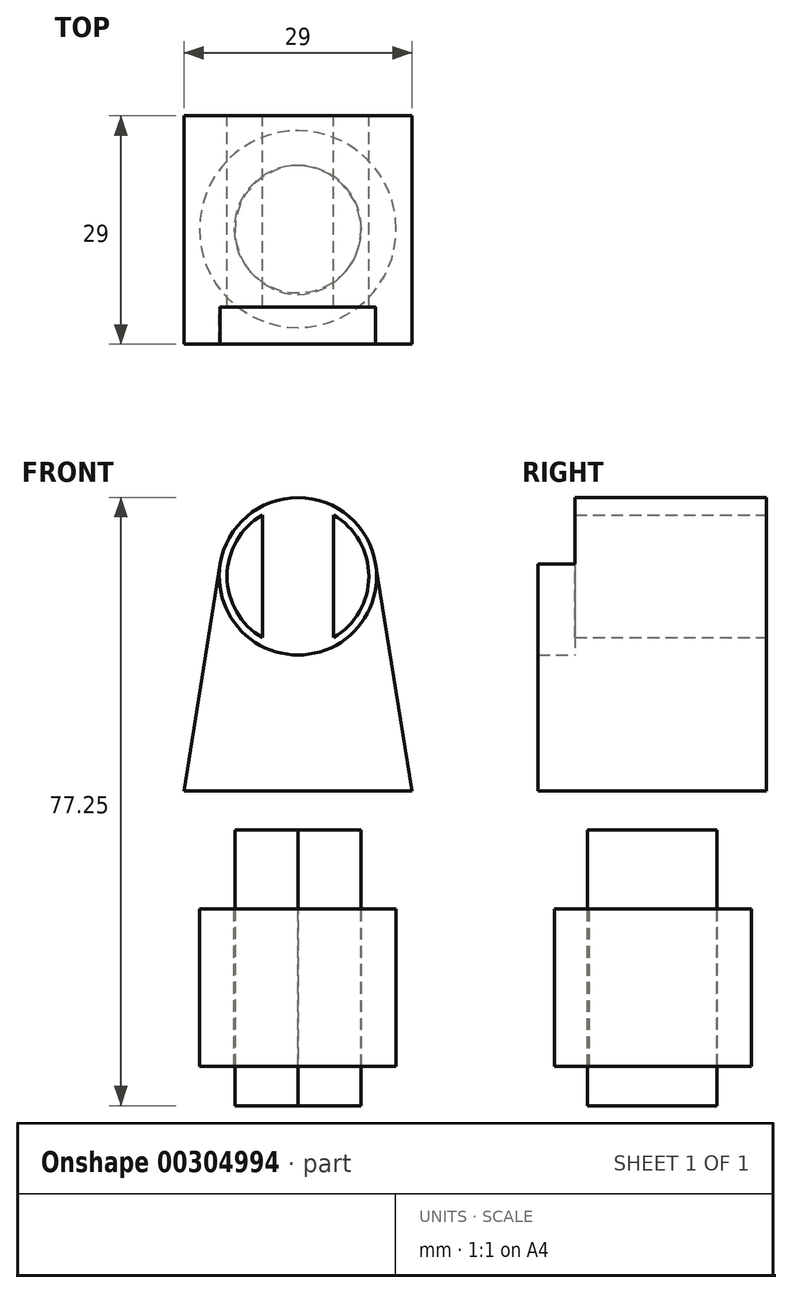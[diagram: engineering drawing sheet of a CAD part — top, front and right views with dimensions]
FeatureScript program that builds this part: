
annotation { "Feature Type Name" : "Feature", "Feature Type Description" : "" }
export const myFeature = defineFeature(function(context is Context, id is Id, definition is map)
    precondition{}
    {
        {
            var Q0;
            Q0=qCreatedBy(makeId("Front.planeOp"),FACE);
            var sketch = newSketch(context, id + "F0", { "sketchPlane" : qUnion([Q0])});
            skLineSegment(sketch, "E0", {"start": v(0, 0) * mm, "end": v(14.5, 0) * mm});
            skLineSegment(sketch, "E1", {"start": v(-14.5, 0) * mm, "end": v(0, 0) * mm});
            skCircle(sketch, "E2", {"center": v(0, 27.25) * mm, "radius": 10 * mm});
            skLineSegment(sketch, "E3", {"start": v(0, 0) * mm, "end": v(8, 0) * mm});
            skLineSegment(sketch, "E4", {"start": v(8, 0) * mm, "end": v(8, -40) * mm});
            skLineSegment(sketch, "E5", {"start": v(8, -40) * mm, "end": v(-8, -40) * mm});
            skLineSegment(sketch, "E6", {"start": v(-8, -40) * mm, "end": v(-8, 0) * mm});
            skLineSegment(sketch, "E7", {"start": v(-8, 0) * mm, "end": v(0, 0) * mm});
            skLineSegment(sketch, "E8", {"start": v(0, 0) * mm, "end": v(8.2, 0) * mm});
            skLineSegment(sketch, "E9", {"start": v(8.2, 0) * mm, "end": v(8.2, -5) * mm});
            skLineSegment(sketch, "E10", {"start": v(8.2, -5) * mm, "end": v(-8, -5) * mm});
            skLineSegment(sketch, "E11", {"start": v(8.2, -5) * mm, "end": v(-8.2, -5) * mm});
            skLineSegment(sketch, "E12", {"start": v(-8.2, -5) * mm, "end": v(-8.2, 0) * mm});
            skLineSegment(sketch, "E13", {"start": v(-8.2, 0) * mm, "end": v(0, 0) * mm});
            skArc(sketch, "E14", {"start": v(-4.5, 35.04) * mm, "mid": v(0, 18.25) * mm, "end": v(4.5, 35.04) * mm});
            skLineSegment(sketch, "E15", {"start": v(4.5, 36.18) * mm, "end": v(4.5, 19.46) * mm});
            skLineSegment(sketch, "E16", {"start": v(-4.5, 19.46) * mm, "end": v(-4.5, 36.18) * mm});
            skLineSegment(sketch, "E17", {"start": v(-14.5, 0) * mm, "end": v(-9.87, 28.83) * mm});
            skLineSegment(sketch, "E18", {"start": v(14.5, 0) * mm, "end": v(9.87, 28.83) * mm});
            skPoint(sketch, "E19.start.orphan", {"position": v(-14.5, 37.25) * mm});
            skPoint(sketch, "E20.start.orphan", {"position": v(0, 37.25) * mm});
            skPoint(sketch, "E21.end.orphan", {"position": v(14.5, 37.25) * mm});
            skSolve(sketch);
        }
        {
            var Q0;
            {var subQ4=sQuery(id+"F0.wireOp",EDGE,"E0");Q0=makeQuery(id+"F0.imprint","IMPRINT",FACE,{"disambiguationData":[TD([[makeQuery(id+"F0.imprint","IMPRINT",EDGE,{"derivedFrom":subQ4}),1.0]])]});}
            extrude(context, id + "F1", {"entities" : qUnion([Q0]), "depth" : 29 * mm});
        }
        {
            var Q0;
            {var subQ0=sQuery(id+"F0.wireOp",EDGE,"E15");var subQ6=sQuery(id+"F0.wireOp",EDGE,"E2");var subQ7=makeQuery(id+"F0.imprint","INTERSECT",VERTEX,{"derivedFrom":[subQ6,subQ0]});Q0=makeQuery(id+"F0.imprint","IMPRINT",FACE,{"disambiguationData":[TD([[makeQuery(id+"F0.imprint","IMPRINT",EDGE,{"disambiguationData":[TD([[subQ7,-1.0]])],"derivedFrom":subQ6}),1.0]])]});}
            extrude(context, id + "F2", {"entities" : qUnion([Q0]), "operationType" : NewBodyOperationType.ADD, "depth" : 18.5 * mm});
        }
        {
            var Q0;
            {var subQ0=sQuery(id+"F0.wireOp",EDGE,"E16");var subQ1=sQuery(id+"F0.wireOp",EDGE,"E14");var subQ2=makeQuery(id+"F0.imprint","INTERSECT",VERTEX,{"disambiguationData":[OD(0.0)],"derivedFrom":[subQ1,subQ0]});Q0=makeQuery(id+"F0.imprint","IMPRINT",FACE,{"disambiguationData":[TD([[makeQuery(id+"F0.imprint","IMPRINT",EDGE,{"disambiguationData":[TD([[subQ2,-1.0]])],"derivedFrom":subQ1}),1.0]])]});}
            var Q1;
            {var subQ0=sQuery(id+"F0.wireOp",EDGE,"E15");var subQ1=sQuery(id+"F0.wireOp",EDGE,"E14");var subQ2=makeQuery(id+"F0.imprint","INTERSECT",VERTEX,{"disambiguationData":[OD(0.0)],"derivedFrom":[subQ1,subQ0]});Q1=makeQuery(id+"F0.imprint","IMPRINT",FACE,{"disambiguationData":[TD([[makeQuery(id+"F0.imprint","IMPRINT",EDGE,{"disambiguationData":[TD([[subQ2,1.0]])],"derivedFrom":subQ1}),1.0]])]});}
            var Q2;
            {var subQ4=sQuery(id+"F0.wireOp",EDGE,"E2");var subQ8=sQuery(id+"F0.wireOp",EDGE,"E15");var subQ9=makeQuery(id+"F0.imprint","INTERSECT",VERTEX,{"derivedFrom":[subQ4,subQ8]});Q2=makeQuery(id+"F0.imprint","IMPRINT",FACE,{"disambiguationData":[TD([[makeQuery(id+"F0.imprint","IMPRINT",EDGE,{"disambiguationData":[TD([[subQ9,1.0]])],"derivedFrom":subQ4}),1.0]])]});}
            extrude(context, id + "F3", {"entities" : qUnion([Q0, Q1, Q2]), "operationType" : NewBodyOperationType.ADD, "depth" : 24.3 * mm});
        }
        {
            var Q0;
            {var subQ0=sQuery(id+"F0.wireOp",EDGE,"E5");Q0=makeQuery(id+"F0.imprint","IMPRINT",FACE,{"disambiguationData":[TD([[makeQuery(id+"F0.imprint","IMPRINT",EDGE,{"derivedFrom":subQ0}),-1.0]])]});}
            var Q1;
            {var subQ1=sQuery(id+"F0.wireOp",EDGE,"E4");var subQ7=sQuery(id+"F0.wireOp",EDGE,"E8");var subQ8=makeQuery(id+"F0.imprint","INTERSECT",VERTEX,{"derivedFrom":[subQ1,subQ7]});Q1=makeQuery(id+"F0.imprint","IMPRINT",FACE,{"disambiguationData":[TD([[makeQuery(id+"F0.imprint","IMPRINT",EDGE,{"disambiguationData":[TD([[subQ8,-1.0]])],"derivedFrom":subQ1}),-1.0]])]});}
            extrude(context, id + "F4", {"entities" : qUnion([Q0, Q1]), "operationType" : NewBodyOperationType.ADD, "depth" : (29 - 6.3) * mm, "hasSecondDirection" : true, "secondDirectionOppositeDirection" : false, "secondDirectionDepth" : 6.3 * mm});
        }
        {
            var Q0;
            Q0=makeQuery(id+"F4.opExtrude","CAP_EDGE",EDGE,{"disambiguationData":[OSD([sQuery(id+"F0.wireOp",EDGE,"E6")])],"isStart":true});
            var Q1;
            Q1=makeQuery(id+"F4.opExtrude","CAP_EDGE",EDGE,{"disambiguationData":[OSD([sQuery(id+"F0.wireOp",EDGE,"E6")])],"isStart":false});
            var Q2;
            Q2=makeQuery(id+"F4.opExtrude","CAP_EDGE",EDGE,{"disambiguationData":[OSD([sQuery(id+"F0.wireOp",EDGE,"E4")])],"isStart":true});
            var Q3;
            Q3=makeQuery(id+"F4.opExtrude","CAP_EDGE",EDGE,{"disambiguationData":[OSD([sQuery(id+"F0.wireOp",EDGE,"E4")])],"isStart":false});
            fillet(context, id + "F5", {"entities" : qUnion([Q0, Q1, Q2, Q3]), "radius" : 8.2 * mm, "tangentPropagation" : true, "allowEdgeOverflow" : false});
        }
        {
            var Q0;
            Q0=qCreatedBy(makeId("Top.planeOp"),FACE);
            var sketch = newSketch(context, id + "F6", { "sketchPlane" : qUnion([Q0])});
            skCircle(sketch, "E22", {"center": v(-0.02, -14.4) * mm, "radius": 8.09 * mm});
            skPoint(sketch, "E22.first.point", {"position": v(-6.47, -19.29) * mm});
            skPoint(sketch, "E22.second.point", {"position": v(7.02, -18.38) * mm});
            skPoint(sketch, "E22.third.point", {"position": v(0, -6.31) * mm});
            skCircle(sketch, "E23", {"center": v(-0.02, -14.4) * mm, "radius": 12.5 * mm});
            skSolve(sketch);
        }
        {
            var Q0;
            Q0=makeQuery(id+"F6.imprint","IMPRINT",FACE,{"disambiguationData":[TD([[makeQuery(id+"F6.imprint","IMPRINT",EDGE,{"derivedFrom":sQuery(id+"F6.wireOp",EDGE,"E22")}),-1.0]])]});
            extrude(context, id + "F7", {"entities" : qUnion([Q0]), "oppositeDirection" : true, "depth" : 35 * mm, "hasSecondDirection" : true, "secondDirectionOppositeDirection" : true, "secondDirectionDepth" : 15 * mm});
        }
    });
